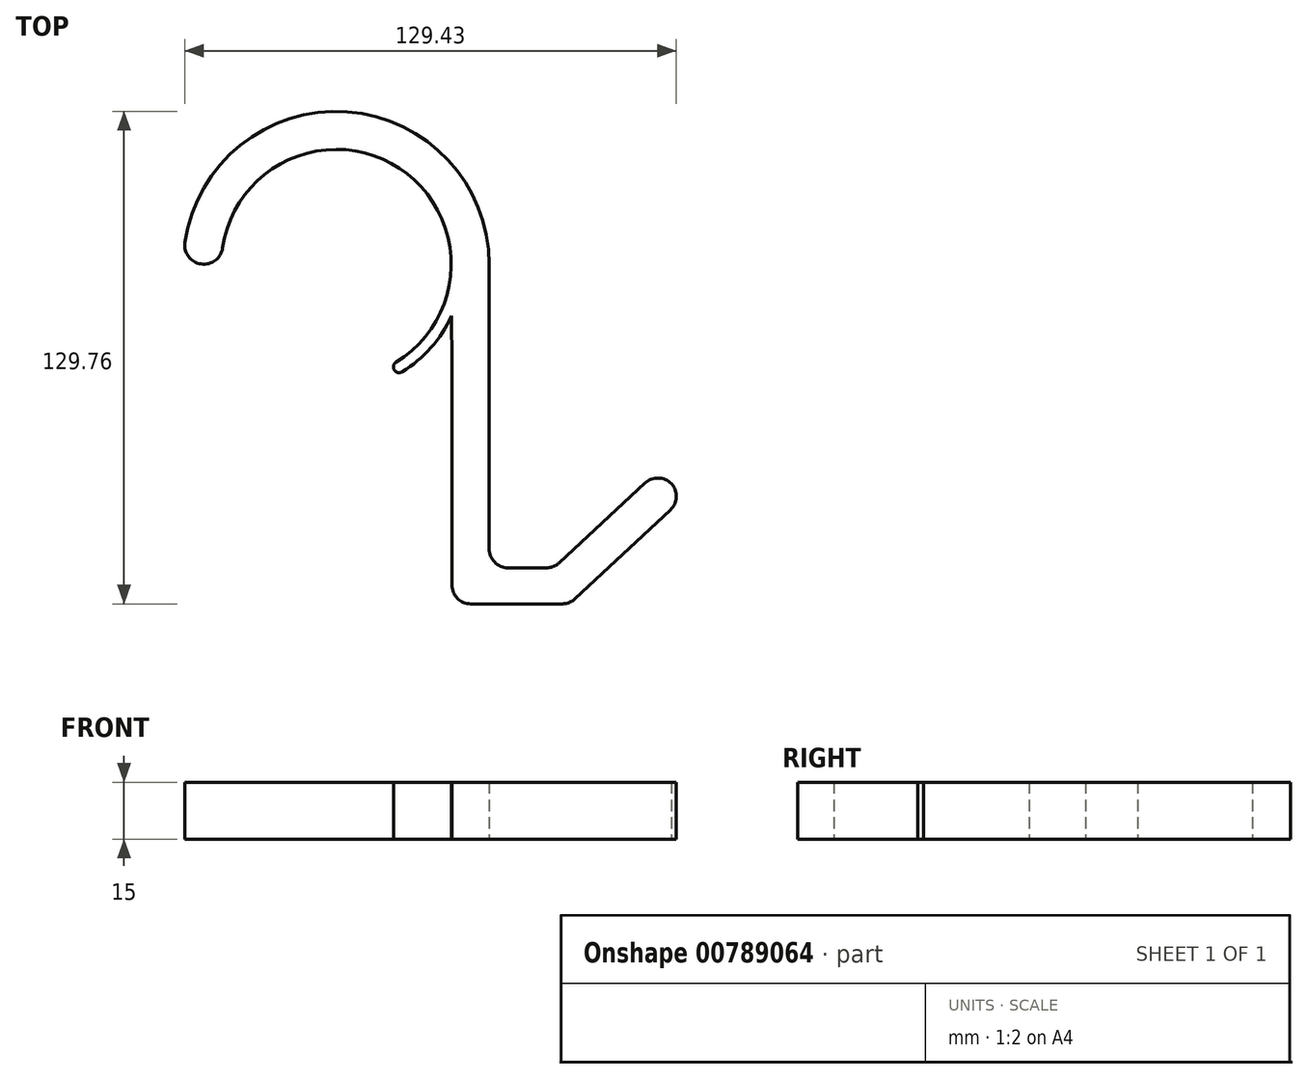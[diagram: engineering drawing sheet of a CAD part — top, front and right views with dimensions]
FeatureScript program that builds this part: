
annotation { "Feature Type Name" : "Feature", "Feature Type Description" : "" }
export const myFeature = defineFeature(function(context is Context, id is Id, definition is map)
    precondition{}
    {
        {
            var Q0;
            Q0=qCreatedBy(makeId("Top.planeOp"),FACE);
            var sketch = newSketch(context, id + "F0", { "sketchPlane" : qUnion([Q0])});
            skArc(sketch, "E0", {"start": v(14.52, -26.54) * mm, "mid": v(15.42, 26.02) * mm, "end": v(-30.25, 0) * mm});
            skLineSegment(sketch, "E1", {"start": v(30.43, -89.5) * mm, "end": v(61.43, -89.5) * mm});
            skLineSegment(sketch, "E2", {"start": v(61.43, -89.5) * mm, "end": v(91.61, -61.43) * mm});
            skLineSegment(sketch, "E3", {"start": v(-30.25, 0) * mm, "end": v(-40.25, 0) * mm});
            skArc(sketch, "E4", {"start": v(15.96, -29.17) * mm, "mid": v(24.4, -22.58) * mm, "end": v(30.32, -13.66) * mm});
            skLineSegment(sketch, "E5", {"start": v(14.52, -26.54) * mm, "end": v(15.96, -29.17) * mm});
            skArc(sketch, "E6", {"start": v(40.25, 0) * mm, "mid": v(0, 40.25) * mm, "end": v(-40.25, 0) * mm});
            skLineSegment(sketch, "E7.0", {"start": v(57.32, -80) * mm, "end": v(84.96, -54.28) * mm});
            skLineSegment(sketch, "E7.1", {"start": v(40.25, -80) * mm, "end": v(57.32, -80) * mm});
            skLineSegment(sketch, "E7.2", {"start": v(40.25, 0) * mm, "end": v(40.25, -80) * mm});
            skLineSegment(sketch, "E8", {"start": v(84.96, -54.28) * mm, "end": v(91.61, -61.43) * mm});
            skLineSegment(sketch, "E9.trimOffspring", {"start": v(30.43, -26.34) * mm, "end": v(30.43, -89.5) * mm});
            skPoint(sketch, "E10.start.orphan", {"position": v(30.25, 0) * mm});
            skLineSegment(sketch, "E11", {"start": v(30.43, -26.34) * mm, "end": v(30.32, -13.66) * mm});
            skSolve(sketch);
        }
        {
            var Q0;
            Q0 = qSketchRegion(id + "F0", true);
            extrude(context, id + "F1", {"entities" : qUnion([Q0]), "depth" : 15 * mm, "offsetDistance" : 25 * mm});
        }
        {
            var Q0;
            Q0=makeQuery(id+"F1.opExtrude","SWEPT_EDGE",EDGE,{"disambiguationData":[OSD([sQuery(id+"F0.wireOp",EDGE,"E0"),sQuery(id+"F0.wireOp",EDGE,"E3")])]});
            var Q1;
            Q1=makeQuery(id+"F1.opExtrude","SWEPT_EDGE",EDGE,{"disambiguationData":[OSD([sQuery(id+"F0.wireOp",EDGE,"E3"),sQuery(id+"F0.wireOp",EDGE,"E6")])]});
            var Q2;
            Q2=makeQuery(id+"F1.opExtrude","SWEPT_EDGE",EDGE,{"disambiguationData":[OSD([sQuery(id+"F0.wireOp",EDGE,"E7.0"),sQuery(id+"F0.wireOp",EDGE,"E8")])]});
            var Q3;
            Q3=makeQuery(id+"F1.opExtrude","SWEPT_EDGE",EDGE,{"disambiguationData":[OSD([sQuery(id+"F0.wireOp",EDGE,"E2"),sQuery(id+"F0.wireOp",EDGE,"E8")])]});
            var Q4;
            Q4=makeQuery(id+"F1.opExtrude","SWEPT_EDGE",EDGE,{"disambiguationData":[OSD([sQuery(id+"F0.wireOp",EDGE,"E1"),sQuery(id+"F0.wireOp",EDGE,"E9.trimOffspring")])]});
            var Q5;
            Q5=makeQuery(id+"F1.opExtrude","SWEPT_EDGE",EDGE,{"disambiguationData":[OSD([sQuery(id+"F0.wireOp",EDGE,"E7.1"),sQuery(id+"F0.wireOp",EDGE,"E7.2")])]});
            var Q6;
            Q6=makeQuery(id+"F1.opExtrude","SWEPT_EDGE",EDGE,{"disambiguationData":[OSD([sQuery(id+"F0.wireOp",EDGE,"E7.0"),sQuery(id+"F0.wireOp",EDGE,"E7.1")])]});
            var Q7;
            Q7=makeQuery(id+"F1.opExtrude","SWEPT_EDGE",EDGE,{"disambiguationData":[OSD([sQuery(id+"F0.wireOp",EDGE,"E1"),sQuery(id+"F0.wireOp",EDGE,"E2")])]});
            fillet(context, id + "F2", {"entities" : qUnion([Q0, Q1, Q2, Q3, Q4, Q5, Q6, Q7]), "radius" : 5 * mm, "tangentPropagation" : true, "allowEdgeOverflow" : false});
        }
        {
            var Q0;
            Q0=makeQuery(id+"F1.opExtrude","SWEPT_EDGE",EDGE,{"disambiguationData":[OSD([sQuery(id+"F0.wireOp",EDGE,"E0"),sQuery(id+"F0.wireOp",EDGE,"E5")])]});
            var Q1;
            Q1=makeQuery(id+"F1.opExtrude","SWEPT_EDGE",EDGE,{"disambiguationData":[OSD([sQuery(id+"F0.wireOp",EDGE,"E4"),sQuery(id+"F0.wireOp",EDGE,"E5")])]});
            fillet(context, id + "F3", {"entities" : qUnion([Q0, Q1]), "radius" : 1.5 * mm, "tangentPropagation" : true, "allowEdgeOverflow" : false});
        }
    });
